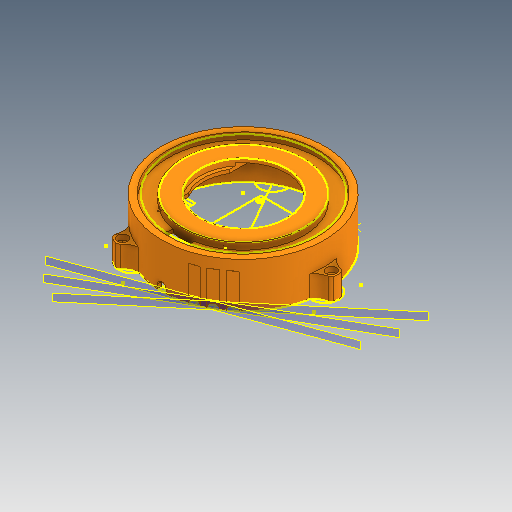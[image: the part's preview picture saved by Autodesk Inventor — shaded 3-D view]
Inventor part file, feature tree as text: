
AUTODESK INVENTOR PART (.ipt)
format: ipt  version: 2020.3 (Build 243373000, 373)  size: 312,320 bytes
history: native  units: mm
features: sketch x9, other x3, plane x3
ambient origin geometry x8: Origin, YZ Plane, XZ Plane, XY Plane, X Axis, Y Axis, Z Axis, Center Point
bodies: Solid1 (feature_tree)
feature tree (15):
  other  "Door-TopPart.ipt"
  other  "Solid2::Door-TopPart.ipt"
  other  "TaggingFeature1"
  sketch  "Sketch1"  dims[d0=10.0mm]
  sketch  "Sketch2"
  sketch  "Sketch3"
  sketch  "Sketch4"
  sketch  "Sketch5"
  sketch  "Sketch6"
  sketch  "Sketch7"
  sketch  "Sketch8"
  sketch  "Sketch9"
  plane  "Work Plane1"
  plane  "Work Plane2"
  plane  "Work Plane3"
